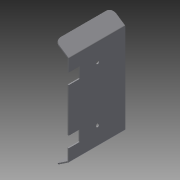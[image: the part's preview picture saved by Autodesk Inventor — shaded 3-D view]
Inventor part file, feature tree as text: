
AUTODESK INVENTOR PART (.ipt)
format: ipt  version: 2015 (Build 190159000, 159)  size: 121,856 bytes
history: native  units: mm
features: extrude x3, sketch x2, fillet x1
ambient origin geometry x8: Origin, YZ Plane, XZ Plane, XY Plane, X Axis, Y Axis, Z Axis, Center Point
bodies: Solid1 (feature_tree)
feature tree (6):
  extrude  "Extrusion1"  Depth=1.0mm
  sketch  "Sketch2"  dims[d5=52.0mm d6=0.0mm d10=3.0mm d11=3.0mm d12=1.0mm d13=0.0mm d14=5.0mm d15=5.0mm d16=10.0mm d17=10.0mm d18=10.0mm d19=10.0mm d20=1.0mm d21=0.0mm d22=5.0mm]
  extrude  "Extrusion2"  Depth=5.0mm
  extrude  "Extrusion3"  Depth=5.0mm
  fillet  "Fillet1"  Radius=1.0mm
  sketch  "Sketch1"  dims[d0=1.0mm d4=1.0mm]
